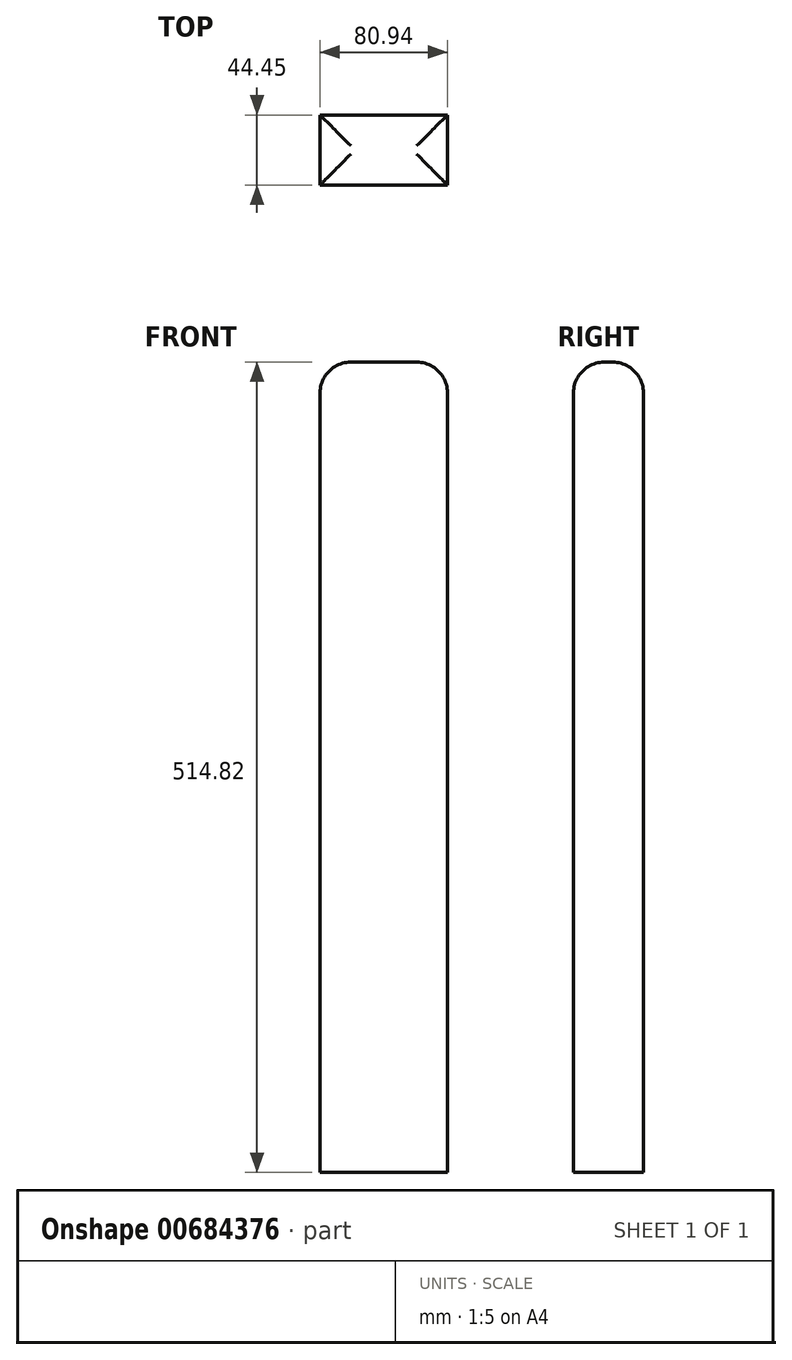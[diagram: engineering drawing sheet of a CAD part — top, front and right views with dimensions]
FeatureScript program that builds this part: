
annotation { "Feature Type Name" : "Feature", "Feature Type Description" : "" }
export const myFeature = defineFeature(function(context is Context, id is Id, definition is map)
    precondition{}
    {
        {
            var Q0;
            Q0=qCreatedBy(makeId("Front.planeOp"),FACE);
            var sketch = newSketch(context, id + "F0", { "sketchPlane" : qUnion([Q0])});
            skLineSegment(sketch, "E0.bottom", {"start": v(-80.94, -37.18) * mm, "end": v(0, -37.18) * mm});
            skLineSegment(sketch, "E0.top", {"start": v(-80.94, 477.64) * mm, "end": v(0, 477.64) * mm});
            skLineSegment(sketch, "E0.left", {"start": v(-80.94, -37.18) * mm, "end": v(-80.94, 477.64) * mm});
            skLineSegment(sketch, "E0.right", {"start": v(0, -37.18) * mm, "end": v(0, 477.64) * mm});
            skSolve(sketch);
        }
        {
            var Q0;
            Q0=makeQuery(id+"F0.imprint","IMPRINT",FACE,{"disambiguationData":[TD([[makeQuery(id+"F0.imprint","IMPRINT",EDGE,{"derivedFrom":sQuery(id+"F0.wireOp",EDGE,"E0.bottom")}),1.0]])]});
            extrude(context, id + "F1", {"entities" : qUnion([Q0]), "depth" : 44.45 * mm, "offsetDistance" : 25.4 * mm});
        }
        {
            var Q0;
            Q0=makeQuery(id+"F1.opExtrude","SWEPT_FACE",FACE,{"disambiguationData":[OSD([sQuery(id+"F0.wireOp",EDGE,"E0.top")])]});
            fillet(context, id + "F2", {"entities" : qUnion([Q0]), "radius" : 19.53 * mm, "tangentPropagation" : true, "allowEdgeOverflow" : false});
        }
        {
            var Q0;
            Q0=makeQuery(id+"F1.opExtrude","SWEPT_FACE",FACE,{"disambiguationData":[OSD([sQuery(id+"F0.wireOp",EDGE,"E0.bottom")])]});
            extrude(context, id + "F3", {"entities" : qUnion([Q0]), "operationType" : NewBodyOperationType.ADD, "oppositeDirection" : true, "depth" : 62.53 * mm, "offsetDistance" : 25.4 * mm});
        }
    });
